# Revit family: 52 Intersan Modus Baby Changer
name_source: partatom
category: Plumbing Fixtures
revit_build: Autodesk Revit 2017 (Build: 20170816_0615(x64)
units: mm (PartAtom-declared; Revit-internal decimal feet)

## family parameters
Always vertical = Yes
Cut with Voids When Loaded = No
OmniClass Number = 23.40.20.21
OmniClass Title = Toilet and Bath Specialties
Part Type = Normal
Room Calculation Point = No
Round Connector Dimension = Use Diameter
Shared = No
Work Plane-Based = No

## types (1)
- Baby Changer
    CW Connection = No
    Drain Diameter = 1 1/2"
    HW Connection = No
    Manufacturer = Intersan
    Material = Anti-microbial Solid Surface and Stainless Steel
    Model = Modus Baby Changer
    Supply Cold Diameter = 1/2"
    Supply Hot Diameter = 1/2"
    Unit Depth = 21 7/8"
    Unit Height = 16"
    Unit Width = 20"
    Warranty = 5 years on material - 3 years on components - 1 year on faucets
    Waste Connection = No
    Water Usage = 0.5 gpm

## geometry (parser evidence)
native form markers: Sweep x3
no freeform markers — native parametric forms only
